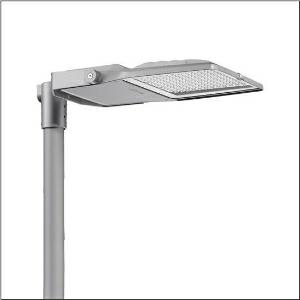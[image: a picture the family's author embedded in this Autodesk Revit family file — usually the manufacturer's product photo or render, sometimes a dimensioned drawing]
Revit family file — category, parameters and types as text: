
# Revit family: floodlight_fl_21_midi___pl61_5xa7785e2c3a_8e59
name_source: partatom
category: Lighting Fixtures
units: mm (PartAtom-declared; Revit-internal decimal feet)

## family parameters
Cut with Voids When Loaded = No
Host = Face
Light Source = No
Part Type = Normal
Room Calculation Point = No
Round Connector Dimension = Use Diameter
Shared = No

## types (1)
- --- (1 x LED, 26450 lm, 212.4 W, 3000K)
    Apparent Load = 212 VA
    CIE Flux Codes = 33 65 98 100 100
    Color Rendering = 70
    Color Temperature = 3000K
    Default Elevation = 1800 mm
    Description = Floodlight FL 21 midi, floodlight, primary light control with lens, of PMMA, primary optical cover: protective disc, of toughened safety glass, transparent, light distribution: PL61, light emission: direct distribution, installation type: surface-mounted, LED, High Power LED, rated luminous flux: 26.450lm, luminous efficacy: 125lm/W, light colour: 730, colour temperature: 3000K, control gear: Smart Interface (Zhaga), control: flexible luminous flux parameterisation, time-dependent luminous flux control, constant luminous flux control, overheat protection, pre-setting: logarithmic dimming characteristic, with terminal, 6-pole, mains connection: 220..240V, AC, 50/60Hz, start of lifetime: 212W, end of service life: 231W, reduction: 95W, luminaire housing, of diecast aluminium, powder-coated, Siteco® metallic grey (DB 702S), corrosivity category C5 mid according to DIN EN ISO 12944, suitable for swimming pools, chlorine-resistant, sealing non-destructively replaceable, please order mast flange separately, mast bracket, of steel, galvanised, powder-coated, Siteco® metallic grey (DB 702S), Smart Interface above, protection rating (complete): IP66, insulation class (complete): insulation class II (safety insulation), certification: CE, ENEC, VDE, protection symbol: D, impact resistance: IK08, permissible operating ambient temperature: -20..+40°C, permissible operating ambient temperature for outdoor applications: -40..+50°C, standard: DIN EN 12944, LABS conformity tested according to VDMA 24364:2018-05, packaging unit: 1 piece

Light Distribution: PL61
    Height = 76 mm
    Lamp = 1 x LED
    Lamp Light Flux = 26450 lm
    Lamp Power = 212.4 W
    Lamp count = 1
    Length = 657 mm
    Luminous efficacy = 125 lm/W
    Manufacturer = Siteco
    ModVariant = No
    Model = 5XA7785E2C3A
    Number of Poles = 1
    OnlyDefault = Yes
    Power Factor = 1
    Product Name = Floodlight FL 21 midi | PL61
    Product group = floodlight | pylon annexe
    ProductGroupID = 6200
    Protection Class = Protection class II
    Protection Degree = IP 66
    RLX_Detail_Level = 1
    RLX_Emergency_Light_Flux = 0 lm
    RLX_Emergency_Type = 0
    RLX_Emergency_Type_DB = No
    RlxData = <blob elided: 153809 chars, md5=e87dd111>
    Socket = socket
    Standby Power = 0 W
    System Light Flux = 26450 lm
    System Power = 212 W
    Type Comments = factory setting: luminous flux: 100 % | dim-lin: 254 | 710 mA
    Type Image = l_1007123.jpg
    URL = http://relux.com
    VarID = @adj_194152
    Voltage = 0 V
    Weight = 0.00 kg
    Width = 442 mm

## geometry (parser evidence)
native form markers: Blend x4, Sweep x14
no freeform markers — native parametric forms only
